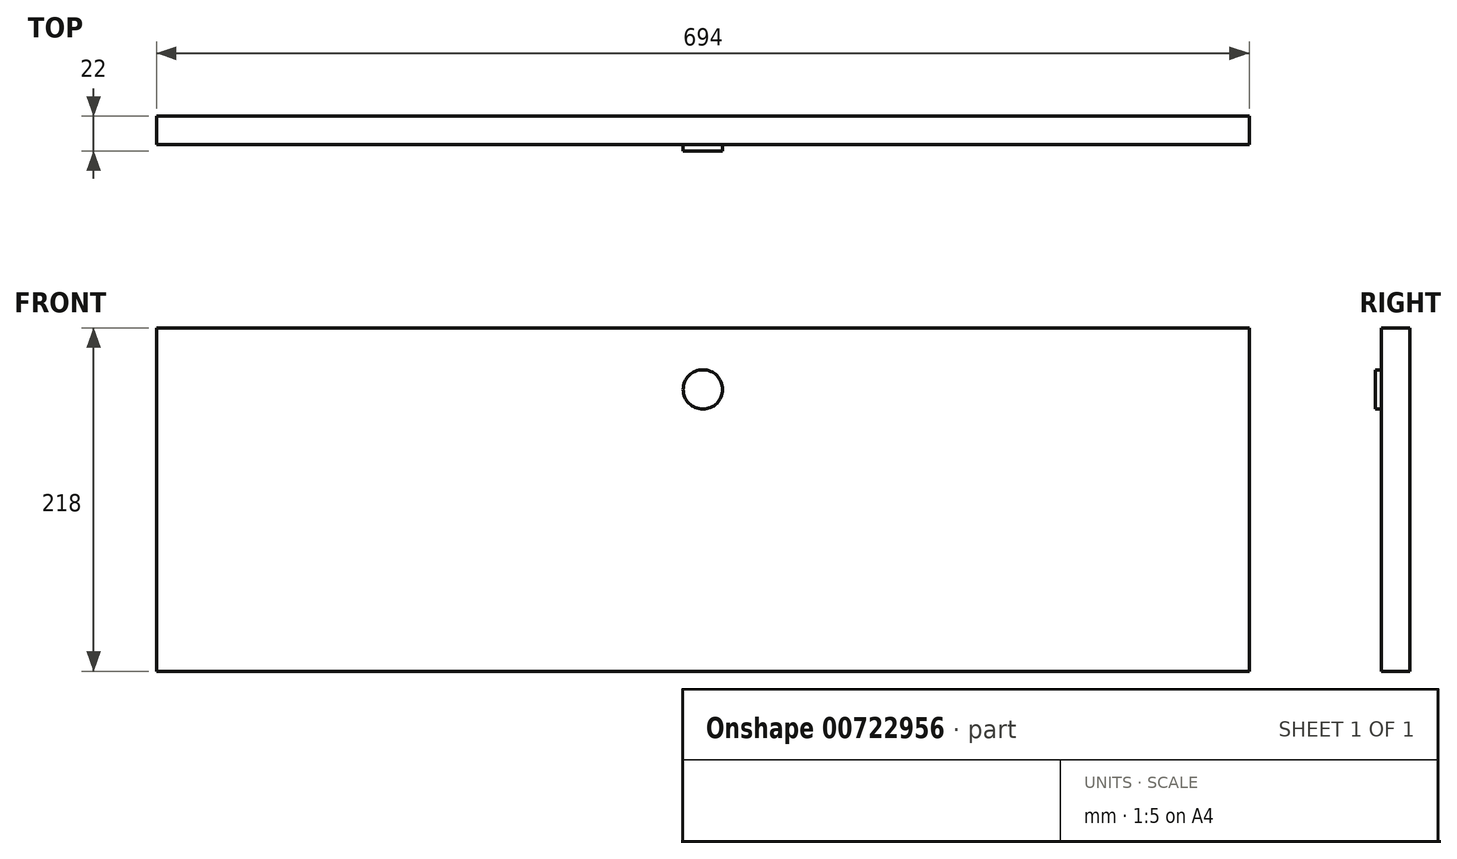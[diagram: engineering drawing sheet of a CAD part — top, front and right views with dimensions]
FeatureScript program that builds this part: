
annotation { "Feature Type Name" : "Feature", "Feature Type Description" : "" }
export const myFeature = defineFeature(function(context is Context, id is Id, definition is map)
    precondition{}
    {
        {
            var Q0;
            Q0=qCreatedBy(makeId("Front.planeOp"),FACE);
            var sketch = newSketch(context, id + "F0", { "sketchPlane" : qUnion([Q0])});
            skLineSegment(sketch, "E0.bottom", {"start": v(-347, 109) * mm, "end": v(347, 109) * mm});
            skLineSegment(sketch, "E0.top", {"start": v(-347, -109) * mm, "end": v(347, -109) * mm});
            skLineSegment(sketch, "E0.left", {"start": v(-347, 109) * mm, "end": v(-347, -109) * mm});
            skLineSegment(sketch, "E0.right", {"start": v(347, 109) * mm, "end": v(347, -109) * mm});
            skLineSegment(sketch, "E1", {"start": v(-347, 109) * mm, "end": v(347, -109) * mm, "construction": true});
            skLineSegment(sketch, "E2", {"start": v(347, 109) * mm, "end": v(-347, -109) * mm, "construction": true});
            skSolve(sketch);
        }
        {
            var Q0;
            Q0 = qSketchRegion(id + "F0", true);
            extrude(context, id + "F1", {"entities" : qUnion([Q0]), "depth" : 18 * mm, "offsetDistance" : 25 * mm});
        }
        {
            var Q0;
            Q0=makeQuery(id+"F1.opExtrude","CAP_FACE",FACE,{"disambiguationData":[OSD([sQuery(id+"F0.wireOp",EDGE,"E0.bottom"),sQuery(id+"F0.wireOp",EDGE,"E0.top"),sQuery(id+"F0.wireOp",EDGE,"E0.left"),sQuery(id+"F0.wireOp",EDGE,"E0.right")])],"isStart":false});
            var sketch = newSketch(context, id + "F2", { "sketchPlane" : qUnion([Q0])});
            skCircle(sketch, "E3", {"center": v(0, 70) * mm, "radius": 12.5 * mm});
            skLineSegment(sketch, "E4", {"start": v(0, 70) * mm, "end": v(0, 0) * mm, "construction": true});
            skSolve(sketch);
        }
        {
            var Q0;
            Q0 = qSketchRegion(id + "F2", true);
            extrude(context, id + "F3", {"entities" : qUnion([Q0]), "operationType" : NewBodyOperationType.ADD, "depth" : 4 * mm, "offsetDistance" : 25 * mm});
        }
    });
